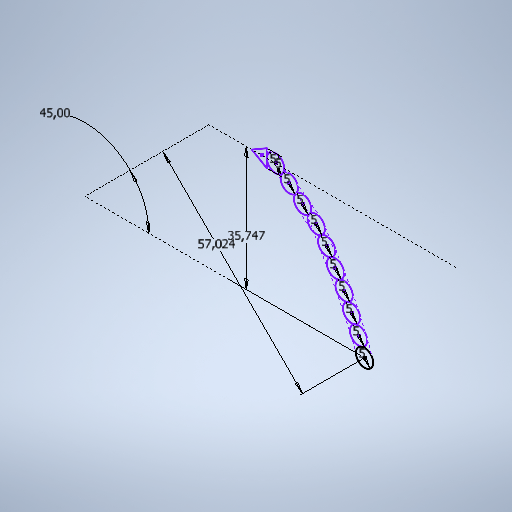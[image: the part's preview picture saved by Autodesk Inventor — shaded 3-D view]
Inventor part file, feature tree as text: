
AUTODESK INVENTOR PART (.ipt)
format: ipt  version: 2025.2 (Build 292293000, 293)  size: 287,744 bytes
history: native  units: mm
features: sketch x1
ambient origin geometry x8: Origin, YZ Plane, XZ Plane, XY Plane, X Axis, Y Axis, Z Axis, Center Point
feature tree (1):
  sketch  "Esboço1"  dims[d0=5.0mm d1=5.0mm d2=5.0mm d3=5.0mm d4=5.0mm d5=5.0mm d6=5.0mm d7=5.0mm d8=5.0mm d9=5.0mm d10=35.747mm d11=57.023886mm d12=45.0deg d13=5.0mm]
